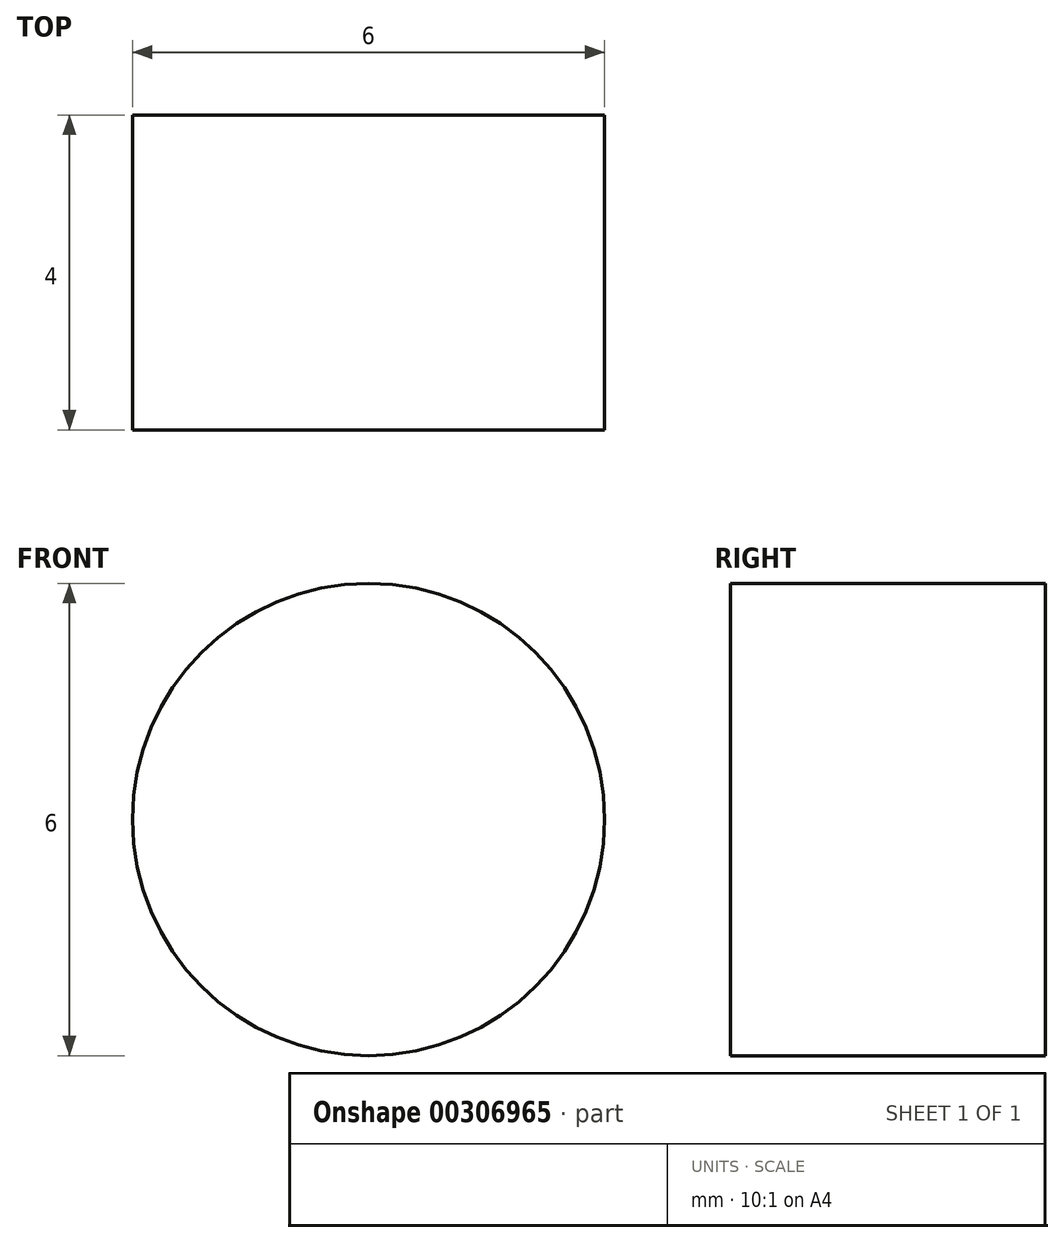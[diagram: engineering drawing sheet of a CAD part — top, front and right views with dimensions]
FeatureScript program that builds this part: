
annotation { "Feature Type Name" : "Feature", "Feature Type Description" : "" }
export const myFeature = defineFeature(function(context is Context, id is Id, definition is map)
    precondition{}
    {
        {
            var Q0;
            Q0=qCreatedBy(makeId("Front.planeOp"),FACE);
            var sketch = newSketch(context, id + "F0", { "sketchPlane" : qUnion([Q0])});
            skCircle(sketch, "E0", {"center": v(0, 0) * mm, "radius": 3 * mm});
            skSolve(sketch);
        }
        {
            var Q0;
            Q0 = qSketchRegion(id + "F0", true);
            extrude(context, id + "F1", {"entities" : qUnion([Q0]), "depth" : 4 * mm});
        }
    });
